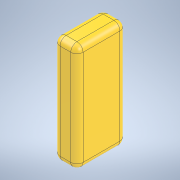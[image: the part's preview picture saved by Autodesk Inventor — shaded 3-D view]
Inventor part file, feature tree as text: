
AUTODESK INVENTOR PART (.ipt)
format: ipt  version: 2021 (Build 250183000, 183)  size: 128,512 bytes
history: native  units: mm
features: extrude x1, fillet x1, sketch x1
ambient origin geometry x8: Origin, YZ Plane, XZ Plane, XY Plane, X Axis, Y Axis, Z Axis, Center Point
bodies: Solid1 (feature_tree)
feature tree (3):
  extrude  "Extrusion1"  Depth=16.0mm
  fillet  "Fillet1"  Radius=35.0mm
  sketch  "Sketch1"  dims[d0=7.5mm d1=16.0mm d2=35.0mm d3=0.0mm d4=2.0mm]
